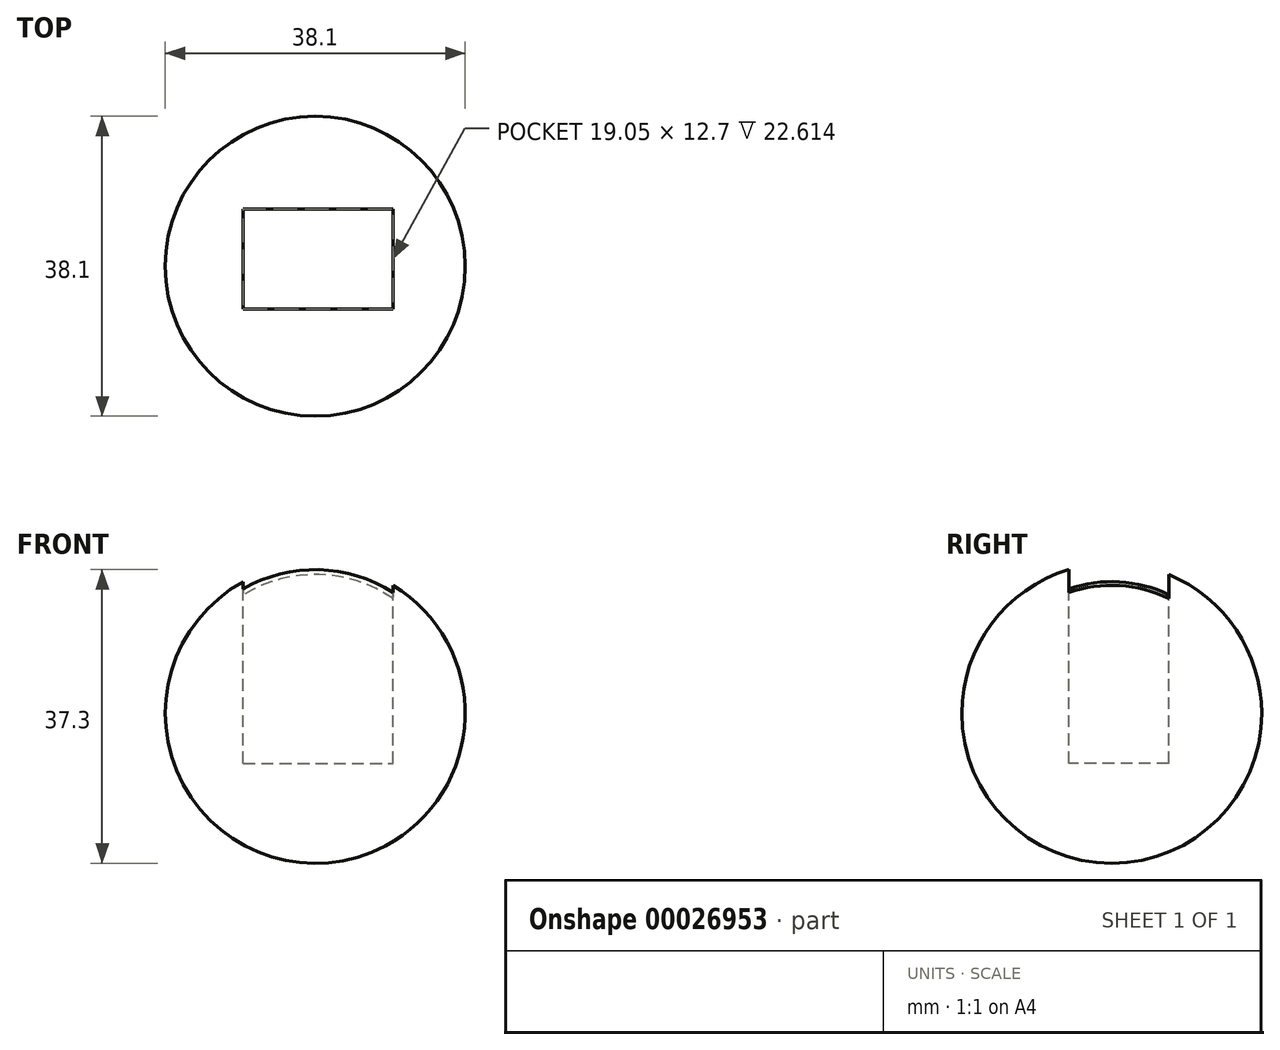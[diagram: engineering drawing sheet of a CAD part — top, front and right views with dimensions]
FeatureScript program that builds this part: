
annotation { "Feature Type Name" : "Feature", "Feature Type Description" : "" }
export const myFeature = defineFeature(function(context is Context, id is Id, definition is map)
    precondition{}
    {
        {
            var Q0;
            Q0=qCreatedBy(makeId("Top.planeOp"),FACE);
            var sketch = newSketch(context, id + "F0", { "sketchPlane" : qUnion([Q0])});
            skLineSegment(sketch, "E0", {"start": v(0, 24.5) * mm, "end": v(0, -13.6) * mm});
            skArc(sketch, "E1", {"start": v(0, -13.6) * mm, "mid": v(19.05, 5.46) * mm, "end": v(0, 24.5) * mm});
            skSolve(sketch);
        }
        {
            var Q0;
            Q0 = qSketchRegion(id + "F0", true);
            var Q1;
            Q1=sQuery(id+"F0.wireOp",EDGE,"E0");
            revolve(context, id + "F1", {"entities" : qUnion([Q0]), "axis" : qUnion([Q1]), "revolveType" : RevolveType.FULL});
        }
        {
            var Q0;
            Q0=qCreatedBy(makeId("Top.planeOp"),FACE);
            cPlane(context, id + "F2", {"entities" : qUnion([Q0]), "cplaneType" : CPlaneType.OFFSET, "offset" : 19.05 * mm, "width" : 152.4 * mm, "height" : 152.4 * mm});
        }
        {
            var Q0;
            Q0=qCreatedBy(id+"F2.planeOp",FACE);
            var sketch = newSketch(context, id + "F3", { "sketchPlane" : qUnion([Q0])});
            skLineSegment(sketch, "E2.bottom", {"start": v(-9.13, 12.7) * mm, "end": v(9.92, 12.7) * mm});
            skLineSegment(sketch, "E2.top", {"start": v(-9.13, 0) * mm, "end": v(9.92, 0) * mm});
            skLineSegment(sketch, "E2.left", {"start": v(-9.13, 12.7) * mm, "end": v(-9.13, 0) * mm});
            skLineSegment(sketch, "E2.right", {"start": v(9.92, 12.7) * mm, "end": v(9.92, 0) * mm});
            skSolve(sketch);
        }
        {
            var Q0;
            Q0=makeQuery(id+"F3.imprint","IMPRINT",FACE,{"disambiguationData":[TD([[makeQuery(id+"F3.imprint","IMPRINT",EDGE,{"derivedFrom":sQuery(id+"F3.wireOp",EDGE,"E2.bottom")}),-1.0]])]});
            extrude(context, id + "F4", {"entities" : qUnion([Q0]), "operationType" : NewBodyOperationType.REMOVE, "oppositeDirection" : true, "depth" : 25.4 * mm});
        }
    });
